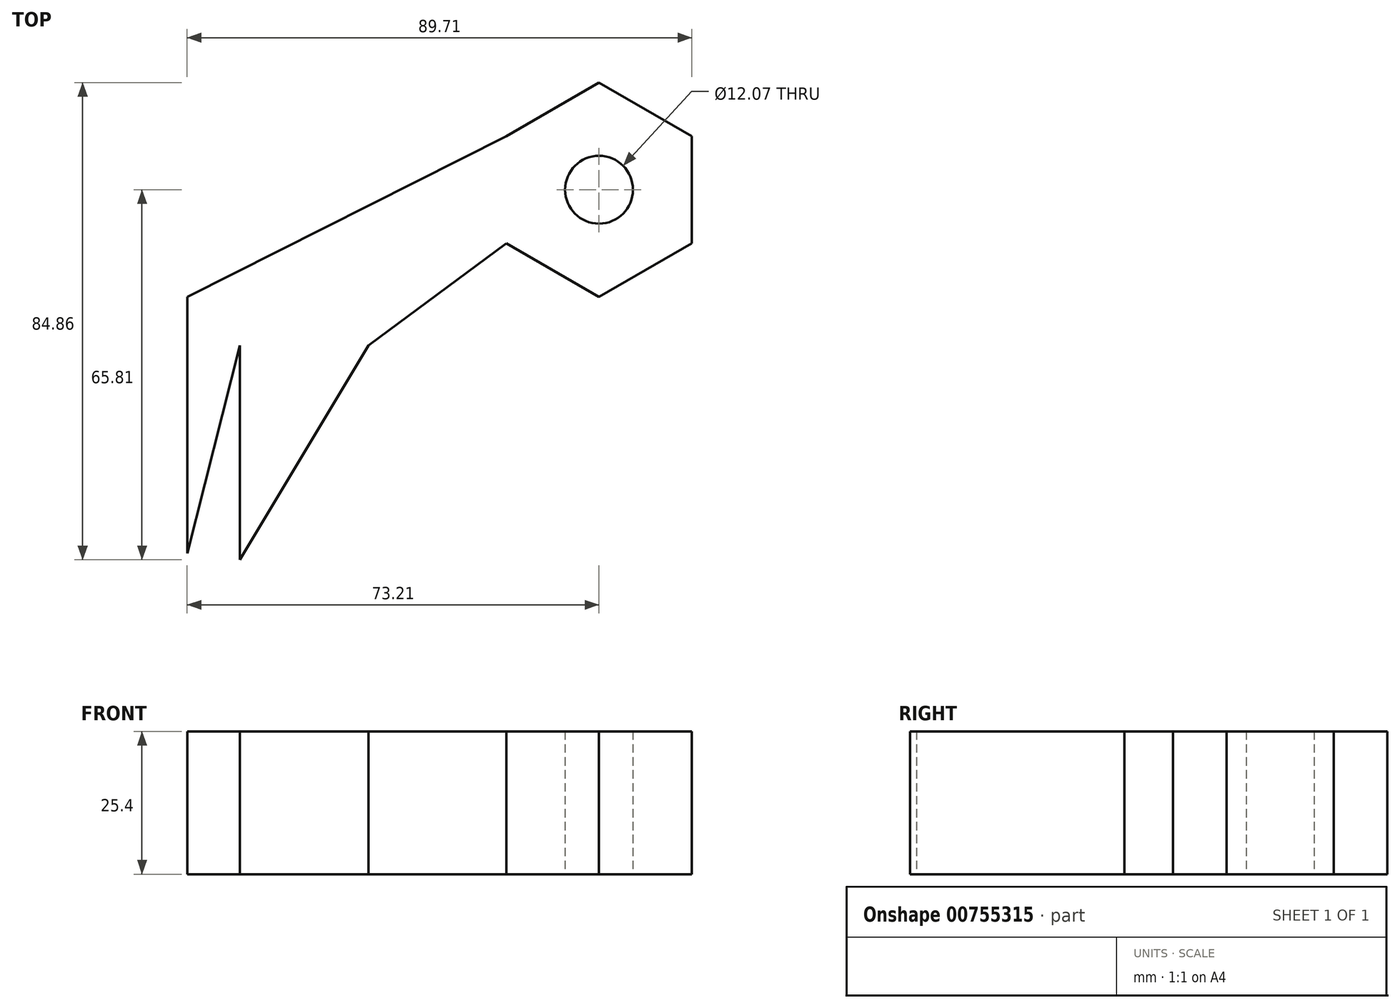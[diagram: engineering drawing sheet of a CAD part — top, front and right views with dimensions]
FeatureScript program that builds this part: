
annotation { "Feature Type Name" : "Feature", "Feature Type Description" : "" }
export const myFeature = defineFeature(function(context is Context, id is Id, definition is map)
    precondition{}
    {
        {
            var Q0;
            Q0=qCreatedBy(makeId("Top.planeOp"),FACE);
            var sketch = newSketch(context, id + "F0", { "sketchPlane" : qUnion([Q0])});
            skLineSegment(sketch, "E0", {"start": v(0, 0) * mm, "end": v(0, 38.1) * mm});
            skLineSegment(sketch, "E1", {"start": v(0, 38.1) * mm, "end": v(76.2, 38.1) * mm});
            skLineSegment(sketch, "E2", {"start": v(76.2, 0) * mm, "end": v(0, 0) * mm});
            skArc(sketch, "E3", {"start": v(76.2, 38.1) * mm, "mid": v(95.25, 19.05) * mm, "end": v(76.2, 0) * mm});
            skCircle(sketch, "E4.cCircle", {"center": v(0, 19.05) * mm, "radius": 19.05 * mm, "construction": true});
            skLineSegment(sketch, "E4.0", {"start": v(0, 0) * mm, "end": v(-16.5, 9.53) * mm});
            skLineSegment(sketch, "E4.1", {"start": v(-16.5, 9.53) * mm, "end": v(-16.5, 28.58) * mm});
            skLineSegment(sketch, "E4.2", {"start": v(-16.5, 28.58) * mm, "end": v(0, 38.1) * mm});
            skLineSegment(sketch, "E4.3", {"start": v(0, 38.1) * mm, "end": v(16.5, 28.58) * mm});
            skLineSegment(sketch, "E4.4", {"start": v(16.5, 28.58) * mm, "end": v(16.5, 9.53) * mm});
            skLineSegment(sketch, "E4.5", {"start": v(16.5, 9.53) * mm, "end": v(0, 0) * mm});
            skLineSegment(sketch, "E5", {"start": v(-16.5, 28.58) * mm, "end": v(-73.2, 0) * mm});
            skLineSegment(sketch, "E6", {"start": v(-73.2, 0) * mm, "end": v(-73.2, -45.6) * mm});
            skLineSegment(sketch, "E7", {"start": v(-73.2, -45.6) * mm, "end": v(-63.85, -8.66) * mm});
            skLineSegment(sketch, "E8", {"start": v(-63.85, -8.66) * mm, "end": v(-63.85, -46.76) * mm});
            skLineSegment(sketch, "E9", {"start": v(-63.85, -46.76) * mm, "end": v(-40.96, -8.66) * mm});
            skLineSegment(sketch, "E10", {"start": v(-40.96, -8.66) * mm, "end": v(-16.5, 9.53) * mm});
            skCircle(sketch, "E11", {"center": v(0, 19.05) * mm, "radius": 6.04 * mm});
            skSolve(sketch);
        }
        {
            var Q0;
            {var subQ0=sQuery(id+"F0.wireOp",EDGE,"E4.3");Q0=makeQuery(id+"F0.imprint","IMPRINT",FACE,{"disambiguationData":[TD([[makeQuery(id+"F0.imprint","IMPRINT",EDGE,{"derivedFrom":subQ0}),-1.0]])]});}
            var Q1;
            {var subQ0=sQuery(id+"F0.wireOp",EDGE,"E4.0");Q1=makeQuery(id+"F0.imprint","IMPRINT",FACE,{"disambiguationData":[TD([[makeQuery(id+"F0.imprint","IMPRINT",EDGE,{"derivedFrom":subQ0}),-1.0]])]});}
            var Q2;
            Q2=makeQuery(id+"F0.imprint","IMPRINT",FACE,{"disambiguationData":[TD([[makeQuery(id+"F0.imprint","IMPRINT",EDGE,{"derivedFrom":sQuery(id+"F0.wireOp",EDGE,"E4.1")}),1.0]])]});
            extrude(context, id + "F1", {"entities" : qUnion([Q0, Q1, Q2]), "depth" : 25.4 * mm, "offsetDistance" : 25.4 * mm});
        }
    });
